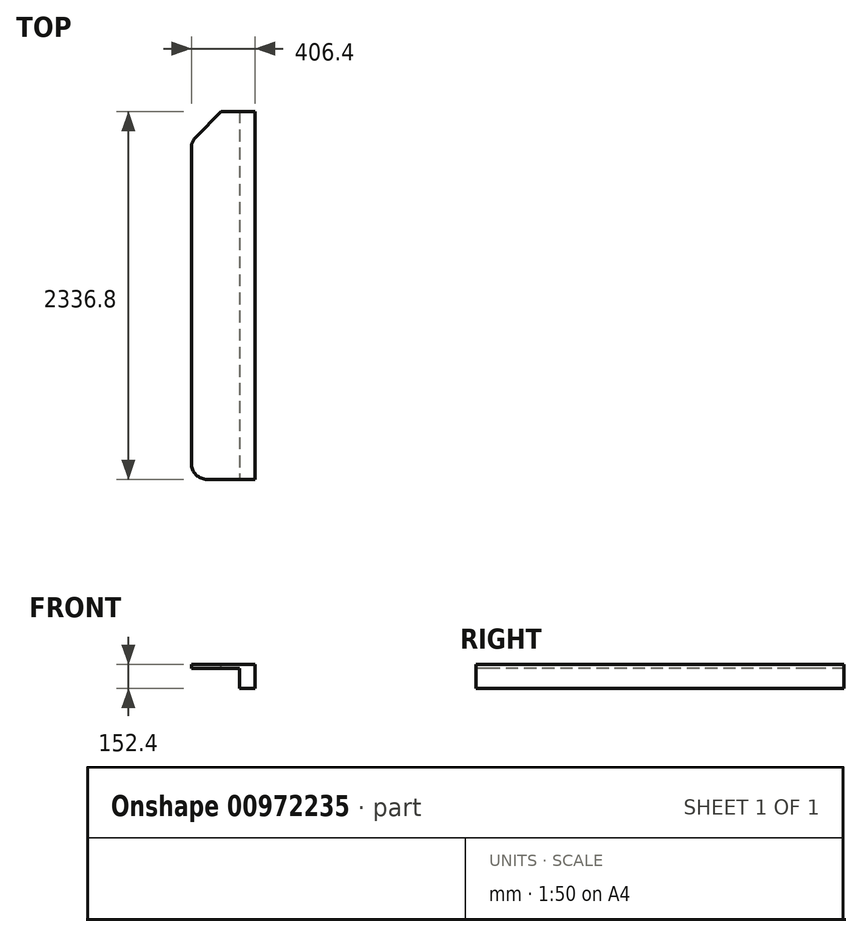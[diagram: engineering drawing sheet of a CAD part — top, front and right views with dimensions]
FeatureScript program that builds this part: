
annotation { "Feature Type Name" : "Feature", "Feature Type Description" : "" }
export const myFeature = defineFeature(function(context is Context, id is Id, definition is map)
    precondition{}
    {
        {
            var Q0;
            Q0=qCreatedBy(makeId("Front.planeOp"),FACE);
            var sketch = newSketch(context, id + "F0", { "sketchPlane" : qUnion([Q0])});
            skLineSegment(sketch, "E0", {"start": v(-406.4, 0) * mm, "end": v(0, 0) * mm});
            skLineSegment(sketch, "E1", {"start": v(0, 0) * mm, "end": v(0, -152.4) * mm});
            skLineSegment(sketch, "E2", {"start": v(0, -152.4) * mm, "end": v(-101.6, -152.4) * mm});
            skLineSegment(sketch, "E3", {"start": v(-101.6, -152.4) * mm, "end": v(-101.6, -25.4) * mm});
            skLineSegment(sketch, "E4", {"start": v(-101.6, -25.4) * mm, "end": v(-406.4, -25.4) * mm});
            skLineSegment(sketch, "E5", {"start": v(-406.4, -25.4) * mm, "end": v(-406.4, 0) * mm});
            skSolve(sketch);
        }
        {
            var Q0;
            Q0 = qSketchRegion(id + "F0", true);
            extrude(context, id + "F1", {"entities" : qUnion([Q0]), "oppositeDirection" : true, "depth" : 2336.8 * mm, "offsetDistance" : 25.4 * mm});
        }
        {
            var Q0;
            Q0=makeQuery(id+"F1.opExtrude","CAP_EDGE",EDGE,{"disambiguationData":[OSD([sQuery(id+"F0.wireOp",EDGE,"E5")])],"isStart":false});
            chamfer(context, id + "F2", {"entities" : qUnion([Q0]), "width" : 190.5 * mm, "tangentPropagation" : true});
        }
        {
            var Q0;
            {var subQ0=sQuery(id+"F0.wireOp",EDGE,"E5");Q0=makeQuery(id+"F2.opChamfer","BLEND_EDGE",EDGE,{"blendedFrom":[makeQuery(id+"F1.opExtrude","CAP_EDGE",EDGE,{"disambiguationData":[OSD([subQ0])],"isStart":false}),makeQuery(id+"F1.opExtrude","SWEPT_FACE",FACE,{"disambiguationData":[OSD([subQ0])]})],"blendedInto":[makeQuery(id+"F1.opExtrude","SWEPT_FACE",FACE,{"disambiguationData":[OSD([subQ0])]})]});}
            var Q1;
            Q1=makeQuery(id+"F1.opExtrude","CAP_EDGE",EDGE,{"disambiguationData":[OSD([sQuery(id+"F0.wireOp",EDGE,"E5")])],"isStart":true});
            fillet(context, id + "F3", {"entities" : qUnion([Q0, Q1]), "radius" : 101.6 * mm, "tangentPropagation" : true, "allowEdgeOverflow" : false});
        }
    });
